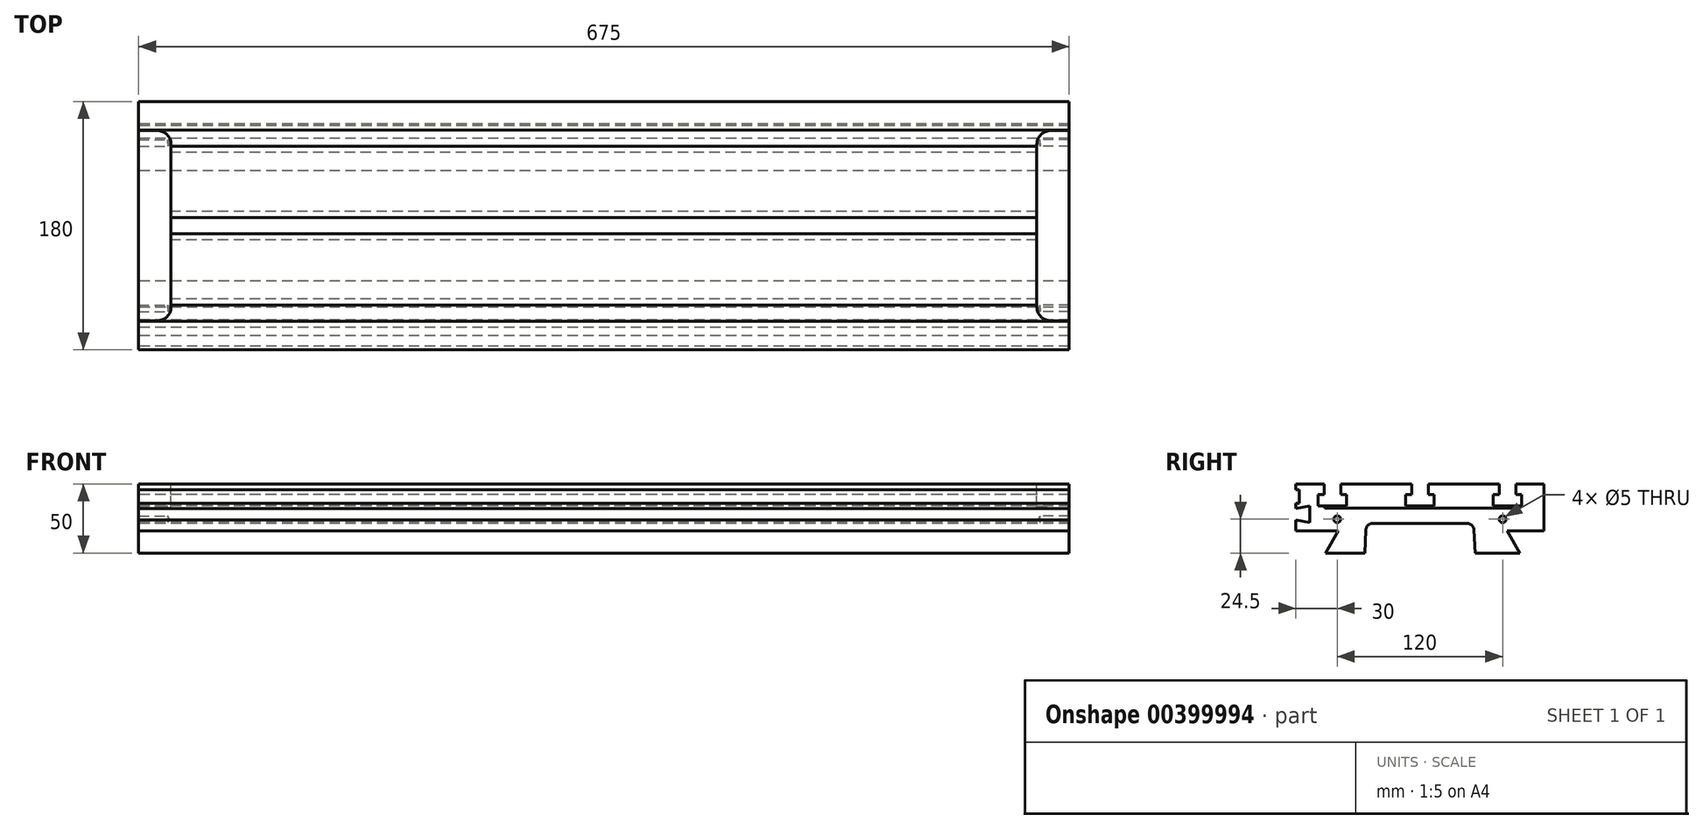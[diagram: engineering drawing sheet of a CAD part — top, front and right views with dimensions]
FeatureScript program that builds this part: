
annotation { "Feature Type Name" : "Feature", "Feature Type Description" : "" }
export const myFeature = defineFeature(function(context is Context, id is Id, definition is map)
    precondition{}
    {
        {
            var Q0;
            Q0=qCreatedBy(makeId("Right.planeOp"),FACE);
            var sketch = newSketch(context, id + "F0", { "sketchPlane" : qUnion([Q0])});
            skLineSegment(sketch, "E0", {"start": v(-90, 36) * mm, "end": v(-90, 32.3) * mm});
            skLineSegment(sketch, "E1", {"start": v(-90, 32.3) * mm, "end": v(-80, 34.15) * mm});
            skLineSegment(sketch, "E2", {"start": v(-80, 34.15) * mm, "end": v(-80, 22.15) * mm});
            skLineSegment(sketch, "E3", {"start": v(-80, 22.15) * mm, "end": v(-90, 24) * mm});
            skLineSegment(sketch, "E4", {"start": v(-90, 24) * mm, "end": v(-90, 16) * mm});
            skLineSegment(sketch, "E5", {"start": v(-90, 16) * mm, "end": v(-59.25, 16) * mm});
            skLineSegment(sketch, "E6", {"start": v(-59.25, 16) * mm, "end": v(-68.49, 0) * mm});
            skLineSegment(sketch, "E7", {"start": v(-68.49, 0) * mm, "end": v(-40, 0) * mm});
            skLineSegment(sketch, "E8", {"start": v(-40, 0) * mm, "end": v(-39.22, 16.73) * mm});
            skLineSegment(sketch, "E9", {"start": v(-34.23, 21.5) * mm, "end": v(34.23, 21.5) * mm});
            skLineSegment(sketch, "E10", {"start": v(39.22, 16.73) * mm, "end": v(40, 0) * mm});
            skLineSegment(sketch, "E11", {"start": v(40, 0) * mm, "end": v(72.49, 0) * mm});
            skLineSegment(sketch, "E12", {"start": v(72.49, 0) * mm, "end": v(63.25, 16) * mm});
            skLineSegment(sketch, "E13", {"start": v(63.25, 16) * mm, "end": v(90, 16) * mm});
            skLineSegment(sketch, "E14", {"start": v(90, 16) * mm, "end": v(90, 50) * mm});
            skLineSegment(sketch, "E15", {"start": v(90, 50) * mm, "end": v(69.5, 50) * mm});
            skLineSegment(sketch, "E16", {"start": v(69.5, 50) * mm, "end": v(69.5, 42.5) * mm});
            skLineSegment(sketch, "E17", {"start": v(69.5, 42.5) * mm, "end": v(73.87, 42.5) * mm});
            skLineSegment(sketch, "E18", {"start": v(73.88, 42.5) * mm, "end": v(73.88, 34) * mm});
            skLineSegment(sketch, "E19", {"start": v(73.88, 34) * mm, "end": v(53.13, 34) * mm});
            skLineSegment(sketch, "E20", {"start": v(53.13, 34) * mm, "end": v(53.13, 42.5) * mm});
            skLineSegment(sketch, "E21", {"start": v(53.13, 42.5) * mm, "end": v(57.5, 42.5) * mm});
            skLineSegment(sketch, "E22", {"start": v(57.5, 42.5) * mm, "end": v(57.5, 50) * mm});
            skLineSegment(sketch, "E23", {"start": v(57.5, 50) * mm, "end": v(6, 50) * mm});
            skLineSegment(sketch, "E24", {"start": v(6, 50) * mm, "end": v(6, 42.5) * mm});
            skLineSegment(sketch, "E25", {"start": v(6, 42.5) * mm, "end": v(10.37, 42.5) * mm});
            skLineSegment(sketch, "E26", {"start": v(10.37, 42.5) * mm, "end": v(10.37, 34) * mm});
            skLineSegment(sketch, "E27", {"start": v(10.37, 34) * mm, "end": v(-10.37, 34) * mm});
            skLineSegment(sketch, "E28", {"start": v(-10.37, 34) * mm, "end": v(-10.37, 42.5) * mm});
            skLineSegment(sketch, "E29", {"start": v(-10.37, 42.5) * mm, "end": v(-6, 42.5) * mm});
            skLineSegment(sketch, "E30", {"start": v(-6, 42.5) * mm, "end": v(-6, 50) * mm});
            skLineSegment(sketch, "E31", {"start": v(-6, 50) * mm, "end": v(-57.5, 50) * mm});
            skLineSegment(sketch, "E32", {"start": v(-57.5, 50) * mm, "end": v(-57.5, 42.5) * mm});
            skLineSegment(sketch, "E33", {"start": v(-57.5, 42.5) * mm, "end": v(-53.13, 42.5) * mm});
            skLineSegment(sketch, "E34", {"start": v(-53.12, 42.5) * mm, "end": v(-53.12, 34) * mm});
            skLineSegment(sketch, "E35", {"start": v(-53.13, 34) * mm, "end": v(-73.88, 34) * mm});
            skLineSegment(sketch, "E36", {"start": v(-73.88, 34) * mm, "end": v(-73.88, 42.5) * mm});
            skLineSegment(sketch, "E37", {"start": v(-73.88, 42.5) * mm, "end": v(-69.5, 42.5) * mm});
            skLineSegment(sketch, "E38", {"start": v(-69.5, 42.5) * mm, "end": v(-69.5, 50) * mm});
            skLineSegment(sketch, "E39", {"start": v(-69.5, 50) * mm, "end": v(-90, 50) * mm});
            skLineSegment(sketch, "E40", {"start": v(-90, 50) * mm, "end": v(-90, 46) * mm});
            skLineSegment(sketch, "E41", {"start": v(-90, 46) * mm, "end": v(-87.5, 46) * mm});
            skLineSegment(sketch, "E42", {"start": v(-87.5, 46) * mm, "end": v(-87.5, 36) * mm});
            skLineSegment(sketch, "E43", {"start": v(-87.5, 36) * mm, "end": v(-90, 36) * mm});
            skLineSegment(sketch, "E44", {"start": v(0, 34) * mm, "end": v(0, 21.5) * mm, "construction": true});
            skLineSegment(sketch, "E45", {"start": v(57.5, 50) * mm, "end": v(69.5, 50) * mm, "construction": true});
            skLineSegment(sketch, "E46", {"start": v(6, 50) * mm, "end": v(-6, 50) * mm, "construction": true});
            skLineSegment(sketch, "E47", {"start": v(-57.5, 50) * mm, "end": v(-69.5, 50) * mm, "construction": true});
            skLineSegment(sketch, "E48", {"start": v(-63.5, 50) * mm, "end": v(-63.5, 34) * mm, "construction": true});
            skLineSegment(sketch, "E49", {"start": v(63.5, 50) * mm, "end": v(63.5, 34) * mm, "construction": true});
            skLineSegment(sketch, "E50", {"start": v(0, 50) * mm, "end": v(0, 34) * mm, "construction": true});
            skPoint(sketch, "E51.visualSharp", {"position": v(-39, 21.5) * mm});
            skArc(sketch, "E51.filletArc", {"start": v(-34.23, 21.5) * mm, "mid": v(-37.68, 20.12) * mm, "end": v(-39.22, 16.73) * mm});
            skPoint(sketch, "E52.visualSharp", {"position": v(39, 21.5) * mm});
            skArc(sketch, "E52.filletArc", {"start": v(39.22, 16.73) * mm, "mid": v(37.68, 20.12) * mm, "end": v(34.23, 21.5) * mm});
            skLineSegment(sketch, "E53", {"start": v(-80, 28.15) * mm, "end": v(-90, 28.15) * mm, "construction": true});
            skSolve(sketch);
        }
        {
            var Q0;
            Q0=qSketchRegion(id+"F0",true);
            extrude(context, id + "F1", {"entities" : qUnion([Q0]), "depth" : 675 * mm, "symmetric" : true});
        }
        {
            var Q0;
            Q0=makeQuery(id+"F1.opExtrude","SWEPT_FACE",FACE,{"disambiguationData":[OSD([sQuery(id+"F0.wireOp",EDGE,"E35")])]});
            var sketch = newSketch(context, id + "F2", { "sketchPlane" : qUnion([Q0])});
            skLineSegment(sketch, "E54.bottom", {"start": v(324, -69) * mm, "end": v(337.5, -69) * mm});
            skLineSegment(sketch, "E54.top", {"start": v(324, 69) * mm, "end": v(337.5, 69) * mm});
            skLineSegment(sketch, "E54.left", {"start": v(314, -59) * mm, "end": v(314, 59) * mm});
            skLineSegment(sketch, "E54.right", {"start": v(337.5, -69) * mm, "end": v(337.5, 69) * mm});
            skLineSegment(sketch, "E55", {"start": v(314, 0) * mm, "end": v(337.5, 0) * mm, "construction": true});
            skPoint(sketch, "E56.visualSharp", {"position": v(314, -69) * mm});
            skArc(sketch, "E56.filletArc", {"start": v(314, -59) * mm, "mid": v(316.93, -66.07) * mm, "end": v(324, -69) * mm});
            skPoint(sketch, "E57.visualSharp", {"position": v(314, 69) * mm});
            skArc(sketch, "E57.filletArc", {"start": v(324, 69) * mm, "mid": v(316.93, 66.07) * mm, "end": v(314, 59) * mm});
            skLineSegment(sketch, "E58", {"start": v(0, 0) * mm, "end": v(0, -90) * mm, "construction": true});
            skPoint(sketch, "E58.endSnap0", {"position": v(0, -73.88) * mm});
            skLineSegment(sketch, "E59.MirrorCS", {"start": v(-314, -59) * mm, "end": v(-314, 59) * mm});
            skArc(sketch, "E60.MirrorCS", {"start": v(-324, 69) * mm, "mid": v(-316.93, 66.07) * mm, "end": v(-314, 59) * mm});
            skLineSegment(sketch, "E61.MirrorCS", {"start": v(-324, 69) * mm, "end": v(-337.5, 69) * mm});
            skLineSegment(sketch, "E62.MirrorCS", {"start": v(-337.5, -69) * mm, "end": v(-337.5, 69) * mm});
            skLineSegment(sketch, "E63.MirrorCS", {"start": v(-324, -69) * mm, "end": v(-337.5, -69) * mm});
            skArc(sketch, "E64.MirrorCS", {"start": v(-314, -59) * mm, "mid": v(-316.93, -66.07) * mm, "end": v(-324, -69) * mm});
            skSolve(sketch);
        }
        {
            var Q0;
            Q0=qSketchRegion(id+"F2",true);
            var Q1;
            Q1=makeQuery(id+"F1.opExtrude","SWEPT_FACE",FACE,{"disambiguationData":[OSD([sQuery(id+"F0.wireOp",EDGE,"E31")])]});
            extrude(context, id + "F3", {"entities" : qUnion([Q0]), "operationType" : NewBodyOperationType.REMOVE, "oppositeDirection" : true, "depth" : 1.5 * mm, "hasSecondDirection" : true, "secondDirectionBound" : BoundingType.UP_TO_SURFACE, "secondDirectionOppositeDirection" : false, "secondDirectionBoundEntityFace" : qUnion([Q1]), "secondDirectionDepth" : 25 * mm});
        }
        {
            var Q0;
            Q0=makeQuery(id+"F1.opExtrude","CAP_FACE",FACE,{"disambiguationData":[OSD([sQuery(id+"F0.wireOp",EDGE,"E0"),sQuery(id+"F0.wireOp",EDGE,"E1"),sQuery(id+"F0.wireOp",EDGE,"E2"),sQuery(id+"F0.wireOp",EDGE,"E3"),sQuery(id+"F0.wireOp",EDGE,"E4"),sQuery(id+"F0.wireOp",EDGE,"E5"),sQuery(id+"F0.wireOp",EDGE,"E6"),sQuery(id+"F0.wireOp",EDGE,"E7"),sQuery(id+"F0.wireOp",EDGE,"E8"),sQuery(id+"F0.wireOp",EDGE,"E9"),sQuery(id+"F0.wireOp",EDGE,"E10"),sQuery(id+"F0.wireOp",EDGE,"E11"),sQuery(id+"F0.wireOp",EDGE,"E12"),sQuery(id+"F0.wireOp",EDGE,"E13"),sQuery(id+"F0.wireOp",EDGE,"E14"),sQuery(id+"F0.wireOp",EDGE,"E15"),sQuery(id+"F0.wireOp",EDGE,"E16"),sQuery(id+"F0.wireOp",EDGE,"E17"),sQuery(id+"F0.wireOp",EDGE,"E18"),sQuery(id+"F0.wireOp",EDGE,"E19"),sQuery(id+"F0.wireOp",EDGE,"E20"),sQuery(id+"F0.wireOp",EDGE,"E21"),sQuery(id+"F0.wireOp",EDGE,"E22"),sQuery(id+"F0.wireOp",EDGE,"E23"),sQuery(id+"F0.wireOp",EDGE,"E24"),sQuery(id+"F0.wireOp",EDGE,"E25"),sQuery(id+"F0.wireOp",EDGE,"E26"),sQuery(id+"F0.wireOp",EDGE,"E27"),sQuery(id+"F0.wireOp",EDGE,"E28"),sQuery(id+"F0.wireOp",EDGE,"E29"),sQuery(id+"F0.wireOp",EDGE,"E30"),sQuery(id+"F0.wireOp",EDGE,"E31"),sQuery(id+"F0.wireOp",EDGE,"E32"),sQuery(id+"F0.wireOp",EDGE,"E33"),sQuery(id+"F0.wireOp",EDGE,"E34"),sQuery(id+"F0.wireOp",EDGE,"E35"),sQuery(id+"F0.wireOp",EDGE,"E36"),sQuery(id+"F0.wireOp",EDGE,"E37"),sQuery(id+"F0.wireOp",EDGE,"E38"),sQuery(id+"F0.wireOp",EDGE,"E39"),sQuery(id+"F0.wireOp",EDGE,"E40"),sQuery(id+"F0.wireOp",EDGE,"E41"),sQuery(id+"F0.wireOp",EDGE,"E42"),sQuery(id+"F0.wireOp",EDGE,"E43"),sQuery(id+"F0.wireOp",EDGE,"E51.filletArc"),sQuery(id+"F0.wireOp",EDGE,"E52.filletArc")])],"isStart":false});
            var sketch = newSketch(context, id + "F4", { "sketchPlane" : qUnion([Q0])});
            skPoint(sketch, "E65", {"position": v(-60, 24.5) * mm});
            skPoint(sketch, "E66", {"position": v(60, 24.5) * mm});
            skLineSegment(sketch, "E67", {"start": v(0, 0) * mm, "end": v(0, 21.5) * mm, "construction": true});
            skSolve(sketch);
        }
        {
            var Q0;
            Q0=sQuery(id+"F4.wireOp",VERTEX,"E65");
            var Q1;
            Q1=sQuery(id+"F4.wireOp",VERTEX,"E66");
            var Q2;
            Q2=makeQuery(id+"F1.opExtrude","SWEPT_BODY",BODY,{"disambiguationData":[OSD([sQuery(id+"F0.wireOp",EDGE,"E0"),sQuery(id+"F0.wireOp",EDGE,"E1"),sQuery(id+"F0.wireOp",EDGE,"E2"),sQuery(id+"F0.wireOp",EDGE,"E3"),sQuery(id+"F0.wireOp",EDGE,"E4"),sQuery(id+"F0.wireOp",EDGE,"E5"),sQuery(id+"F0.wireOp",EDGE,"E6"),sQuery(id+"F0.wireOp",EDGE,"E7"),sQuery(id+"F0.wireOp",EDGE,"E8"),sQuery(id+"F0.wireOp",EDGE,"E9"),sQuery(id+"F0.wireOp",EDGE,"E10"),sQuery(id+"F0.wireOp",EDGE,"E11"),sQuery(id+"F0.wireOp",EDGE,"E12"),sQuery(id+"F0.wireOp",EDGE,"E13"),sQuery(id+"F0.wireOp",EDGE,"E14"),sQuery(id+"F0.wireOp",EDGE,"E15"),sQuery(id+"F0.wireOp",EDGE,"E16"),sQuery(id+"F0.wireOp",EDGE,"E17"),sQuery(id+"F0.wireOp",EDGE,"E18"),sQuery(id+"F0.wireOp",EDGE,"E19"),sQuery(id+"F0.wireOp",EDGE,"E20"),sQuery(id+"F0.wireOp",EDGE,"E21"),sQuery(id+"F0.wireOp",EDGE,"E22"),sQuery(id+"F0.wireOp",EDGE,"E23"),sQuery(id+"F0.wireOp",EDGE,"E24"),sQuery(id+"F0.wireOp",EDGE,"E25"),sQuery(id+"F0.wireOp",EDGE,"E26"),sQuery(id+"F0.wireOp",EDGE,"E27"),sQuery(id+"F0.wireOp",EDGE,"E28"),sQuery(id+"F0.wireOp",EDGE,"E29"),sQuery(id+"F0.wireOp",EDGE,"E30"),sQuery(id+"F0.wireOp",EDGE,"E31"),sQuery(id+"F0.wireOp",EDGE,"E32"),sQuery(id+"F0.wireOp",EDGE,"E33"),sQuery(id+"F0.wireOp",EDGE,"E34"),sQuery(id+"F0.wireOp",EDGE,"E35"),sQuery(id+"F0.wireOp",EDGE,"E36"),sQuery(id+"F0.wireOp",EDGE,"E37"),sQuery(id+"F0.wireOp",EDGE,"E38"),sQuery(id+"F0.wireOp",EDGE,"E39"),sQuery(id+"F0.wireOp",EDGE,"E40"),sQuery(id+"F0.wireOp",EDGE,"E41"),sQuery(id+"F0.wireOp",EDGE,"E42"),sQuery(id+"F0.wireOp",EDGE,"E43"),sQuery(id+"F0.wireOp",EDGE,"E51.filletArc"),sQuery(id+"F0.wireOp",EDGE,"E52.filletArc")])]});
            hole(context, id + "F5", {"style" : HoleStyle.SIMPLE, "endStyle" : HoleEndStyle.BLIND, "standardTappedOrClearance" : lookupTablePath({ "standard" : "ISO", "engagement" : "75%", "pitch" : "1 mm", "size" : "M6", "type" : "Tapped" }), "standardBlindInLast" : lookupTablePath({ "standard" : "ISO", "engagement" : "75%", "pitch" : "1 mm", "size" : "M6", "type" : "Tapped" }), "holeDiameter" : 5 * mm, "showTappedDepth" : true, "holeDepth" : 21 * mm, "isTappedThrough" : true, "tappedDepth" : 18 * mm, "tapClearance" : 3, "locations" : qUnion([Q0, Q1]), "scope" : qUnion([Q2]), "majorDiameter" : 6 * mm, "startStyle" : HoleStartStyle.SKETCH});
        }
        {
            var Q0;
            Q0=makeQuery(id+"F1.opExtrude","CAP_FACE",FACE,{"disambiguationData":[OSD([sQuery(id+"F0.wireOp",EDGE,"E0"),sQuery(id+"F0.wireOp",EDGE,"E1"),sQuery(id+"F0.wireOp",EDGE,"E2"),sQuery(id+"F0.wireOp",EDGE,"E3"),sQuery(id+"F0.wireOp",EDGE,"E4"),sQuery(id+"F0.wireOp",EDGE,"E5"),sQuery(id+"F0.wireOp",EDGE,"E6"),sQuery(id+"F0.wireOp",EDGE,"E7"),sQuery(id+"F0.wireOp",EDGE,"E8"),sQuery(id+"F0.wireOp",EDGE,"E9"),sQuery(id+"F0.wireOp",EDGE,"E10"),sQuery(id+"F0.wireOp",EDGE,"E11"),sQuery(id+"F0.wireOp",EDGE,"E12"),sQuery(id+"F0.wireOp",EDGE,"E13"),sQuery(id+"F0.wireOp",EDGE,"E14"),sQuery(id+"F0.wireOp",EDGE,"E15"),sQuery(id+"F0.wireOp",EDGE,"E16"),sQuery(id+"F0.wireOp",EDGE,"E17"),sQuery(id+"F0.wireOp",EDGE,"E18"),sQuery(id+"F0.wireOp",EDGE,"E19"),sQuery(id+"F0.wireOp",EDGE,"E20"),sQuery(id+"F0.wireOp",EDGE,"E21"),sQuery(id+"F0.wireOp",EDGE,"E22"),sQuery(id+"F0.wireOp",EDGE,"E23"),sQuery(id+"F0.wireOp",EDGE,"E24"),sQuery(id+"F0.wireOp",EDGE,"E25"),sQuery(id+"F0.wireOp",EDGE,"E26"),sQuery(id+"F0.wireOp",EDGE,"E27"),sQuery(id+"F0.wireOp",EDGE,"E28"),sQuery(id+"F0.wireOp",EDGE,"E29"),sQuery(id+"F0.wireOp",EDGE,"E30"),sQuery(id+"F0.wireOp",EDGE,"E31"),sQuery(id+"F0.wireOp",EDGE,"E32"),sQuery(id+"F0.wireOp",EDGE,"E33"),sQuery(id+"F0.wireOp",EDGE,"E34"),sQuery(id+"F0.wireOp",EDGE,"E35"),sQuery(id+"F0.wireOp",EDGE,"E36"),sQuery(id+"F0.wireOp",EDGE,"E37"),sQuery(id+"F0.wireOp",EDGE,"E38"),sQuery(id+"F0.wireOp",EDGE,"E39"),sQuery(id+"F0.wireOp",EDGE,"E40"),sQuery(id+"F0.wireOp",EDGE,"E41"),sQuery(id+"F0.wireOp",EDGE,"E42"),sQuery(id+"F0.wireOp",EDGE,"E43"),sQuery(id+"F0.wireOp",EDGE,"E51.filletArc"),sQuery(id+"F0.wireOp",EDGE,"E52.filletArc")])],"isStart":true});
            var sketch = newSketch(context, id + "F6", { "sketchPlane" : qUnion([Q0])});
            skPoint(sketch, "E68", {"position": v(-60, 24.5) * mm});
            skPoint(sketch, "E69", {"position": v(60, 24.5) * mm});
            skSolve(sketch);
        }
        {
            var Q0;
            Q0=sQuery(id+"F6.wireOp",VERTEX,"E68");
            var Q1;
            Q1=sQuery(id+"F6.wireOp",VERTEX,"E69");
            var Q2;
            Q2=makeQuery(id+"F1.opExtrude","SWEPT_BODY",BODY,{"disambiguationData":[OSD([sQuery(id+"F0.wireOp",EDGE,"E0"),sQuery(id+"F0.wireOp",EDGE,"E1"),sQuery(id+"F0.wireOp",EDGE,"E2"),sQuery(id+"F0.wireOp",EDGE,"E3"),sQuery(id+"F0.wireOp",EDGE,"E4"),sQuery(id+"F0.wireOp",EDGE,"E5"),sQuery(id+"F0.wireOp",EDGE,"E6"),sQuery(id+"F0.wireOp",EDGE,"E7"),sQuery(id+"F0.wireOp",EDGE,"E8"),sQuery(id+"F0.wireOp",EDGE,"E9"),sQuery(id+"F0.wireOp",EDGE,"E10"),sQuery(id+"F0.wireOp",EDGE,"E11"),sQuery(id+"F0.wireOp",EDGE,"E12"),sQuery(id+"F0.wireOp",EDGE,"E13"),sQuery(id+"F0.wireOp",EDGE,"E14"),sQuery(id+"F0.wireOp",EDGE,"E15"),sQuery(id+"F0.wireOp",EDGE,"E16"),sQuery(id+"F0.wireOp",EDGE,"E17"),sQuery(id+"F0.wireOp",EDGE,"E18"),sQuery(id+"F0.wireOp",EDGE,"E19"),sQuery(id+"F0.wireOp",EDGE,"E20"),sQuery(id+"F0.wireOp",EDGE,"E21"),sQuery(id+"F0.wireOp",EDGE,"E22"),sQuery(id+"F0.wireOp",EDGE,"E23"),sQuery(id+"F0.wireOp",EDGE,"E24"),sQuery(id+"F0.wireOp",EDGE,"E25"),sQuery(id+"F0.wireOp",EDGE,"E26"),sQuery(id+"F0.wireOp",EDGE,"E27"),sQuery(id+"F0.wireOp",EDGE,"E28"),sQuery(id+"F0.wireOp",EDGE,"E29"),sQuery(id+"F0.wireOp",EDGE,"E30"),sQuery(id+"F0.wireOp",EDGE,"E31"),sQuery(id+"F0.wireOp",EDGE,"E32"),sQuery(id+"F0.wireOp",EDGE,"E33"),sQuery(id+"F0.wireOp",EDGE,"E34"),sQuery(id+"F0.wireOp",EDGE,"E35"),sQuery(id+"F0.wireOp",EDGE,"E36"),sQuery(id+"F0.wireOp",EDGE,"E37"),sQuery(id+"F0.wireOp",EDGE,"E38"),sQuery(id+"F0.wireOp",EDGE,"E39"),sQuery(id+"F0.wireOp",EDGE,"E40"),sQuery(id+"F0.wireOp",EDGE,"E41"),sQuery(id+"F0.wireOp",EDGE,"E42"),sQuery(id+"F0.wireOp",EDGE,"E43"),sQuery(id+"F0.wireOp",EDGE,"E51.filletArc"),sQuery(id+"F0.wireOp",EDGE,"E52.filletArc")])]});
            hole(context, id + "F7", {"style" : HoleStyle.SIMPLE, "endStyle" : HoleEndStyle.BLIND, "standardTappedOrClearance" : lookupTablePath({ "standard" : "ISO", "engagement" : "75%", "pitch" : "1 mm", "size" : "M6", "type" : "Tapped" }), "standardBlindInLast" : lookupTablePath({ "standard" : "ISO", "engagement" : "75%", "pitch" : "1 mm", "size" : "M6", "type" : "Tapped" }), "holeDiameter" : 5 * mm, "showTappedDepth" : true, "holeDepth" : 21 * mm, "isTappedThrough" : true, "tappedDepth" : 18 * mm, "tapClearance" : 3, "locations" : qUnion([Q0, Q1]), "scope" : qUnion([Q2]), "majorDiameter" : 6 * mm, "startStyle" : HoleStartStyle.SKETCH});
        }
    });
